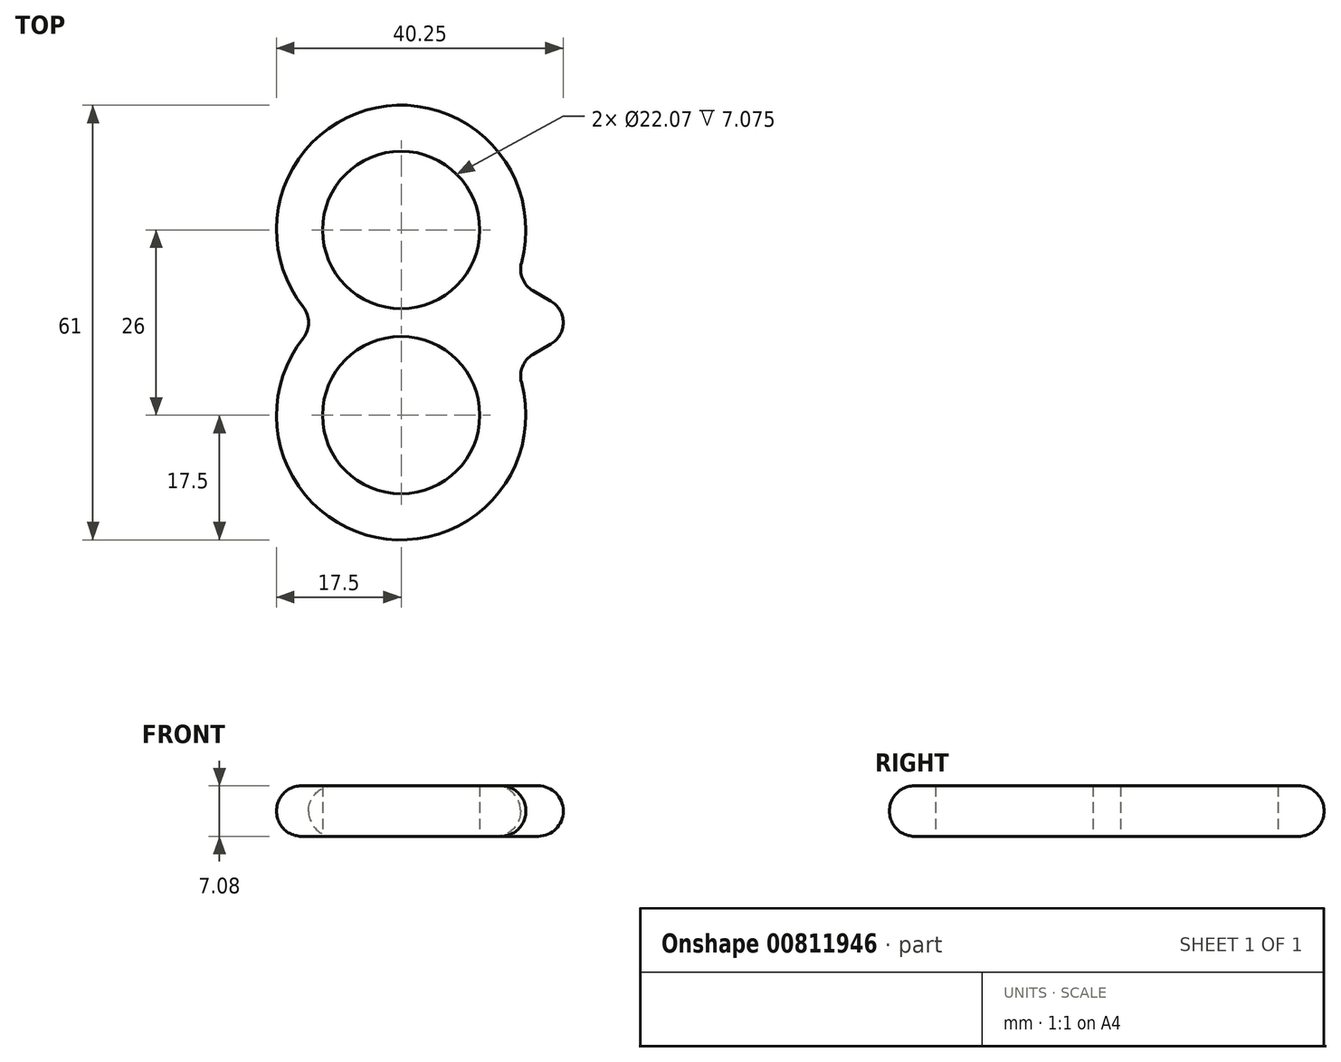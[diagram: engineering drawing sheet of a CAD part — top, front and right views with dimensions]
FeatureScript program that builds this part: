
annotation { "Feature Type Name" : "Feature", "Feature Type Description" : "" }
export const myFeature = defineFeature(function(context is Context, id is Id, definition is map)
    precondition{}
    {
        {
            var Q0;
            Q0=qCreatedBy(makeId("Top.planeOp"),FACE);
            var sketch = newSketch(context, id + "F0", { "sketchPlane" : qUnion([Q0])});
            skCircle(sketch, "E0", {"center": v(0, 13) * mm, "radius": 17.5 * mm});
            skCircle(sketch, "E1", {"center": v(0, -13) * mm, "radius": 17.5 * mm});
            skSolve(sketch);
        }
        {
            var Q0;
            {var subQ0=sQuery(id+"F0.wireOp",EDGE,"E1");var subQ1=sQuery(id+"F0.wireOp",EDGE,"E0");var subQ2=makeQuery(id+"F0.imprint","INTERSECT",VERTEX,{"disambiguationData":[OD(0.0)],"derivedFrom":[subQ1,subQ0]});Q0=makeQuery(id+"F0.imprint","IMPRINT",FACE,{"disambiguationData":[TD([[makeQuery(id+"F0.imprint","IMPRINT",EDGE,{"disambiguationData":[TD([[subQ2,1.0]])],"derivedFrom":subQ1}),1.0]])]});}
            var Q1;
            {var subQ0=sQuery(id+"F0.wireOp",EDGE,"E1");var subQ1=sQuery(id+"F0.wireOp",EDGE,"E0");var subQ2=makeQuery(id+"F0.imprint","INTERSECT",VERTEX,{"disambiguationData":[OD(0.0)],"derivedFrom":[subQ1,subQ0]});Q1=makeQuery(id+"F0.imprint","IMPRINT",FACE,{"disambiguationData":[TD([[makeQuery(id+"F0.imprint","IMPRINT",EDGE,{"disambiguationData":[TD([[subQ2,-1.0]])],"derivedFrom":subQ1}),-1.0]])]});}
            var Q2;
            {var subQ0=sQuery(id+"F0.wireOp",EDGE,"E1");var subQ1=sQuery(id+"F0.wireOp",EDGE,"E0");var subQ2=makeQuery(id+"F0.imprint","INTERSECT",VERTEX,{"disambiguationData":[OD(0.0)],"derivedFrom":[subQ1,subQ0]});Q2=makeQuery(id+"F0.imprint","IMPRINT",FACE,{"disambiguationData":[TD([[makeQuery(id+"F0.imprint","IMPRINT",EDGE,{"disambiguationData":[TD([[subQ2,-1.0]])],"derivedFrom":subQ1}),1.0]])]});}
            extrude(context, id + "F1", {"entities" : qUnion([Q0, Q1, Q2]), "depth" : 7.08 * mm, "offsetDistance" : 25 * mm});
        }
        {
            var Q0;
            Q0=qCreatedBy(makeId("Top.planeOp"),FACE);
            var sketch = newSketch(context, id + "F2", { "sketchPlane" : qUnion([Q0])});
            skCircle(sketch, "E2.cCircle", {"center": v(8.75, 0) * mm, "radius": 8.75 * mm, "construction": true});
            skLineSegment(sketch, "E2.0", {"start": v(0, 15.16) * mm, "end": v(26.25, 0) * mm});
            skLineSegment(sketch, "E2.1", {"start": v(26.25, 0) * mm, "end": v(0, -15.16) * mm});
            skLineSegment(sketch, "E2.2", {"start": v(0, -15.16) * mm, "end": v(0, 15.16) * mm});
            skPoint(sketch, "E2.0.midPoint", {"position": v(13.13, 7.58) * mm});
            skCircle(sketch, "E3.cCircle", {"center": v(-8.75, 0) * mm, "radius": 8.75 * mm, "construction": true});
            skLineSegment(sketch, "E3.0", {"start": v(0, 15.16) * mm, "end": v(0, -15.16) * mm});
            skLineSegment(sketch, "E3.1", {"start": v(0, -15.16) * mm, "end": v(-26.25, 0) * mm});
            skLineSegment(sketch, "E3.2", {"start": v(-26.25, 0) * mm, "end": v(0, 15.16) * mm});
            skPoint(sketch, "E3.0.midPoint", {"position": v(0, 0) * mm});
            skSolve(sketch);
        }
        {
            var Q0;
            Q0=makeQuery(id+"F2.imprint","IMPRINT",FACE,{"disambiguationData":[TD([[makeQuery(id+"F2.imprint","IMPRINT",EDGE,{"derivedFrom":sQuery(id+"F2.wireOp",EDGE,"E3.0")}),-1.0]])]});
            var Q1;
            Q1=makeQuery(id+"F2.imprint","IMPRINT",FACE,{"disambiguationData":[TD([[makeQuery(id+"F2.imprint","IMPRINT",EDGE,{"derivedFrom":sQuery(id+"F2.wireOp",EDGE,"E2.0")}),-1.0]])]});
            extrude(context, id + "F3", {"entities" : qUnion([Q0, Q1]), "operationType" : NewBodyOperationType.ADD, "depth" : 7.08 * mm, "offsetDistance" : 25 * mm});
        }
        {
            var Q0;
            Q0=sQuery(id+"F0.wireOp",VERTEX,"E0.center");
            var Q1;
            Q1=sQuery(id+"F0.wireOp",VERTEX,"E1.center");
            var Q2;
            Q2=makeQuery(id+"F1.opExtrude","SWEPT_BODY",BODY,{"disambiguationData":[OSD([sQuery(id+"F0.wireOp",EDGE,"E0"),sQuery(id+"F0.wireOp",EDGE,"E1")])]});
            hole(context, id + "F4", {"style" : HoleStyle.SIMPLE, "endStyle" : HoleEndStyle.BLIND, "oppositeDirection" : true, "holeDiameter" : 22.07 * mm, "majorDiameter" : 5 * mm, "holeDepth" : 35.38 * mm, "isTappedThrough" : true, "tappedDepth" : 12 * mm, "tapClearance" : 3, "locations" : qUnion([Q0, Q1]), "scope" : qUnion([Q2])});
        }
        {
            var Q0;
            Q0=makeQuery(id+"F3.opExtrude","SWEPT_FACE",FACE,{"disambiguationData":[OSD([sQuery(id+"F2.wireOp",EDGE,"E2.1")])]});
            var Q1;
            Q1=makeQuery(id+"F3.opExtrude","SWEPT_FACE",FACE,{"disambiguationData":[OSD([sQuery(id+"F2.wireOp",EDGE,"E3.1")])]});
            var Q2;
            Q2=makeQuery(id+"F1.opExtrude","SWEPT_FACE",FACE,{"disambiguationData":[OSD([sQuery(id+"F0.wireOp",EDGE,"E0")])]});
            var Q3;
            Q3=makeQuery(id+"F1.opExtrude","SWEPT_FACE",FACE,{"disambiguationData":[OSD([sQuery(id+"F0.wireOp",EDGE,"E1")])]});
            var Q4;
            Q4=makeQuery(id+"F3.opExtrude","SWEPT_FACE",FACE,{"disambiguationData":[OSD([sQuery(id+"F2.wireOp",EDGE,"E2.0")])]});
            var Q5;
            Q5=makeQuery(id+"F3.opExtrude","SWEPT_FACE",FACE,{"disambiguationData":[OSD([sQuery(id+"F2.wireOp",EDGE,"E3.2")])]});
            fillet(context, id + "F5", {"entities" : qUnion([Q0, Q1, Q2, Q3, Q4, Q5]), "radius" : 3.5 * mm, "tangentPropagation" : true, "allowEdgeOverflow" : false});
        }
    });
